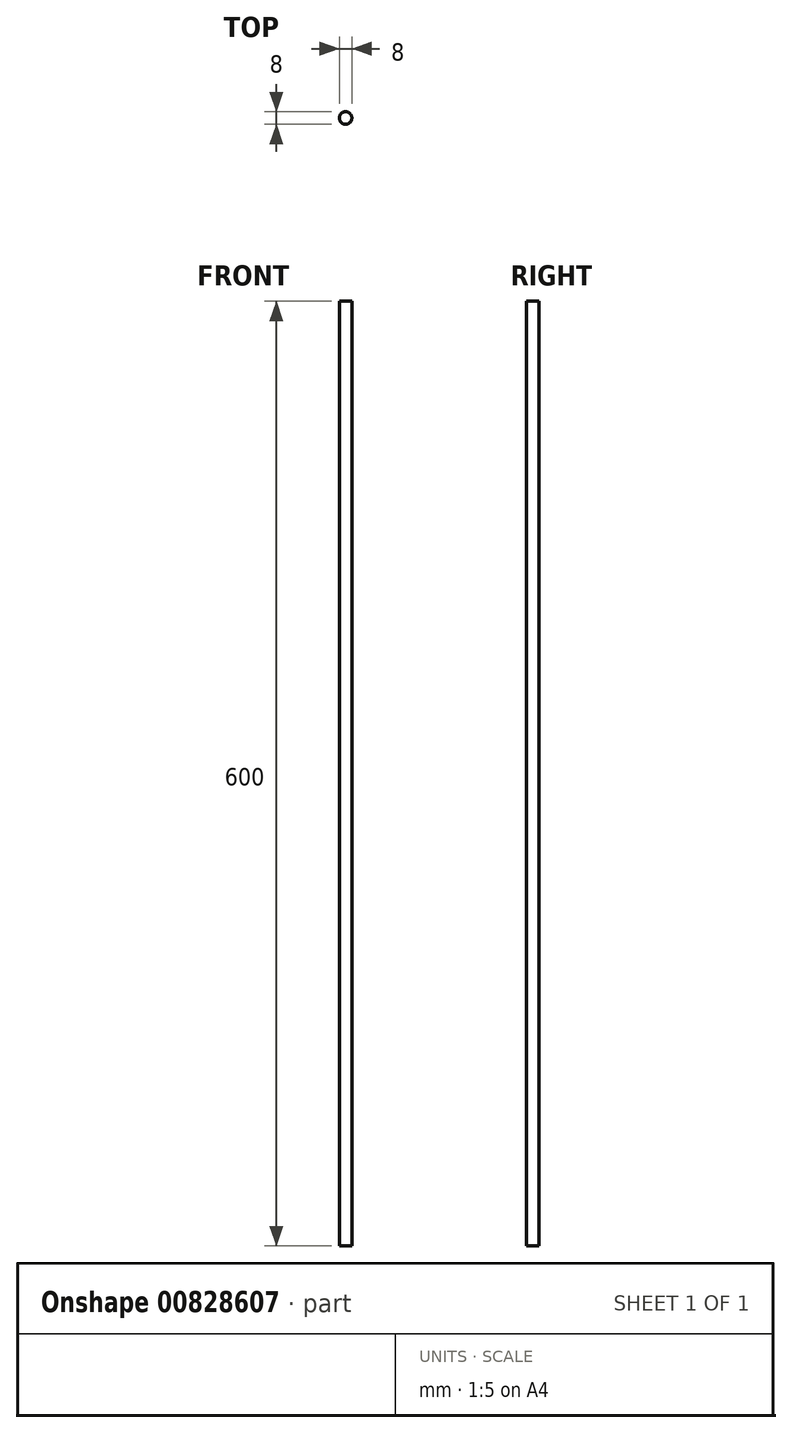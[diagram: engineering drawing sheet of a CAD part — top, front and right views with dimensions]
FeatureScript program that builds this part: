
annotation { "Feature Type Name" : "Feature", "Feature Type Description" : "" }
export const myFeature = defineFeature(function(context is Context, id is Id, definition is map)
    precondition{}
    {
        {
            var Q0;
            Q0=qCreatedBy(makeId("Top.planeOp"),FACE);
            var sketch = newSketch(context, id + "F0", { "sketchPlane" : qUnion([Q0])});
            skCircle(sketch, "E0", {"center": v(0, 0) * mm, "radius": 4 * mm});
            skSolve(sketch);
        }
        {
            var Q0;
            Q0=makeQuery(id+"F0.imprint","IMPRINT",FACE,{"disambiguationData":[TD([[makeQuery(id+"F0.imprint","IMPRINT",EDGE,{"derivedFrom":sQuery(id+"F0.wireOp",EDGE,"E0")}),1.0]])]});
            extrude(context, id + "F1", {"entities" : qUnion([Q0]), "endBound" : BoundingType.SYMMETRIC, "depth" : 600 * mm, "offsetDistance" : 25 * mm});
        }
    });
